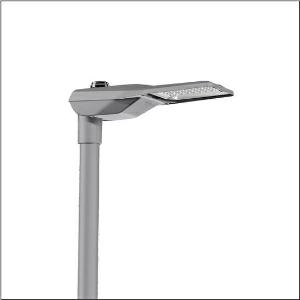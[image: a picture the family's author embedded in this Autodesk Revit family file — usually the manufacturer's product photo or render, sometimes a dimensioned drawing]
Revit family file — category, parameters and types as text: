
# Revit family: streetlight_sl_21_mini___st0_8a_5xe6c37n08hb_0120
name_source: partatom
category: Lighting Fixtures
units: mm (PartAtom-declared; Revit-internal decimal feet)

## family parameters
Cut with Voids When Loaded = No
Host = Face
Light Source = No
Part Type = Normal
Room Calculation Point = No
Round Connector Dimension = Use Diameter
Shared = No

## types (1)
- --- (1 x LED, 9040 lm, 66 W, 3000K)
    Apparent Load = 66 VA
    CIE Flux Codes = 38 75 97 100 100
    Color Rendering = 70
    Color Temperature = 3000K
    Default Elevation = 1800 mm
    Description = Streetlight SL 21 mini, mast luminaire, primary light control with lens, of PMMA, primary optical cover: cover, of toughened safety glass, transparent, light distribution: ST0.8a, light emission: direct distribution, primary light characteristic: asymmetric, installation type: side-entry, LED, 3G 1.5mm², High Power LED, rated luminous flux: 9.040lm, luminous efficacy: 137lm/W, light colour: 730, colour temperature: 3000K, control gear: NEMA (7pin), control: overheat protection, pre-setting: linear dimming characteristic, constant luminous flux control, time-dependent luminous flux control, flexible luminous flux parameterisation, mains connection: 230..240V, AC, 50/60Hz, connection cable pre-assembled, cable length: 8,5m, wiring characteristics: H07RN-F, start of lifetime: 66W, end of service life: 69W, reduction: 30W, luminaire housing, of diecast aluminium (EN AC-44300), powder-coated, SITECO metallic grey (DB 702S), corrosivity category C5 high according to DIN EN ISO 12944, multi-level sealing system, sealing non-destructively replaceable, inclination adjustable: 0°, 5°, 10°, 15°, length: 628mm, width: 235mm, height: 110mm, spigot size: 42mm (side-entry), mounting height: 4..8m, protection rating (complete): IP66, insulation class (complete): insulation class I (protective earthing), certification: CE, ENEC, ENEC+, VDE, impact resistance: IK10, permissible operating ambient temperature for outdoor applications: -40..+50°C, standard-compliant lighting for roads and squares, packaging unit: 1 piece

Light Distribution: ST0.8a
    Height = 110 mm
    Lamp = 1 x LED
    Lamp Light Flux = 9040 lm
    Lamp Power = 66 W
    Lamp count = 1
    Length = 625 mm
    Luminous efficacy = 137 lm/W
    Manufacturer = Siteco
    ModVariant = No
    Model = 5XE6C37N08HB
    Mounting Place = Pole
    Mounting Type = Pole top
    Number of Poles = 1
    OnlyDefault = Yes
    Power Factor = 1
    Product Name = Streetlight SL 21 mini | ST0.8a
    Product group = mast luminaire | pylon top
    ProductGroupID = 6100
    Protection Class = Protection class I
    Protection Degree = IP 66
    RLX_Detail_Level = 1
    RLX_Emergency_Light_Flux = 0 lm
    RLX_Emergency_Type = 0
    RLX_Emergency_Type_DB = No
    RlxData = <blob elided: 26233 chars, md5=df47df03>
    Socket = socket
    Standby Power = 0 W
    System Light Flux = 9040 lm
    System Power = 66 W
    Type Comments = factory setting: luminous flux: 100 % | dim-lin: 254 | 670 mA
    Type Image = l_1294379.jpg
    URL = http://relux.com
    VarID = @adj_135277
    Voltage = 0 V
    Weight = 0.00 kg
    Width = 234 mm

## geometry (parser evidence)
native form markers: Blend x4, Sweep x12
no freeform markers — native parametric forms only
